# Revit family: 210_af9f45931e8442728642362a2fa429
name_source: partatom
category: Mechanical Equipment
revit_build: Autodesk Revit 2018 (Build: 20170223_1515(x64)
units: mm (PartAtom-declared; Revit-internal decimal feet)

## family parameters
Always vertical = Yes
Classification = None
Cut with Voids When Loaded = No
Part Type = Breaks Into
Room Calculation Point = No
Round Connector Dimension = Use Diameter
Shared = No
Work Plane-Based = No

## types (10) — shared parameters
Description = Roof fan DVA EC
Manufacturer = Flexit
QmdConnectorList = 201;D;201;D
SW2 = No
URL = www.flexit.no
W = 500 mm
magiPartTypeId = 210
magiProductFamilyId = af9f45931e8442728642362a2fa429

## per-type parameters (varying)
| type | D | L | X1 | X2 | X3 | Y1 | Y2 | Y3 | Z1 | Z2 | Z3 | Z4 | Z5 | magiProductId |
| 180-114667 | 180 mm | 337 mm | 152 mm | 194 mm  [stored 0.636483 ft] | 175 mm | 63 mm | 80 mm | 72 mm | 19 mm  [stored 0.062336 ft] | 48 mm | 10 mm  [stored 0.0328084 ft] | 8 mm  [stored 0.0262467 ft] | 106 mm | 5af6edb60cd94c0c9996466fb9cec5 |
| 180-114668 | 180 mm | 337 mm | 152 mm | 194 mm  [stored 0.636483 ft] | 175 mm | 63 mm | 80 mm | 72 mm | 19 mm  [stored 0.062336 ft] | 48 mm | 10 mm  [stored 0.0328084 ft] | 8 mm  [stored 0.0262467 ft] | 106 mm | 4df34c234bad4f829b0616fb9199dc |
| 180-114669 | 180 mm | 337 mm | 152 mm | 194 mm  [stored 0.636483 ft] | 175 mm | 63 mm | 80 mm | 72 mm | 19 mm  [stored 0.062336 ft] | 48 mm | 10 mm  [stored 0.0328084 ft] | 8 mm  [stored 0.0262467 ft] | 106 mm | 32e9393b2db04a0da2dc5b05595d94 |
| 250-114670 | 250 mm | 437 mm | 197 mm | 271 mm | 243 mm | 81 mm | 112 mm | 101 mm | 25 mm  [stored 0.082021 ft] | 62 mm | 12 mm  [stored 0.0393701 ft] | 10 mm  [stored 0.0328084 ft] | 139 mm | a07ea9faa7434097bf1e8e56774247 |
| 400-114671 | 400 mm | 598 mm | 269 mm | 373 mm | 335 mm | 111 mm | 154 mm | 139 mm | 33 mm | 83 mm | 17 mm | 13 mm | 186 mm | 4b130bd8c6c44ce49a5a29d3a0bf2f |
| 400-114672 | 400 mm | 598 mm | 269 mm | 373 mm | 335 mm | 111 mm | 154 mm | 139 mm | 33 mm | 83 mm | 17 mm | 13 mm | 186 mm | 6dc5825a987e427a830cf0b7cf0edb |
| 400-114673 | 400 mm | 670 mm | 302 mm | 430 mm | 387 mm | 125 mm | 178 mm | 160 mm  [stored 0.524934 ft] | 42 mm | 105 mm | 21 mm | 17 mm | 234 mm | 156234b6e41049f38bb420cbce9815 |
| 400-114674 | 400 mm | 670 mm | 302 mm | 430 mm | 387 mm | 125 mm | 178 mm | 160 mm  [stored 0.524934 ft] | 42 mm | 105 mm | 21 mm | 17 mm | 234 mm | aee2da43e6eb42659dc6a404c8de67 |
| 560-114675 | 560 mm | 931 mm | 419 mm | 583 mm | 524 mm | 174 mm | 241 mm | 217 mm | 52 mm  [stored 0.170604 ft] | 130 mm | 26 mm | 21 mm | 292 mm | 3d9e01e0c71e49e0b3a0015929caf3 |
| 560-114676 | 560 mm | 931 mm | 419 mm | 583 mm | 524 mm | 174 mm | 241 mm | 217 mm | 52 mm  [stored 0.170604 ft] | 130 mm | 26 mm | 21 mm | 292 mm | 0849a86d8b35461b9c47925c0f168d |

note: column(s) folded — value = type name in every type: MC Product Code

note: [stored X ft] marks values corroborated as IEEE doubles in the binary element streams (Revit-internal decimal feet)

## geometry (parser evidence)
native form markers: Sweep x1
no freeform markers — native parametric forms only
